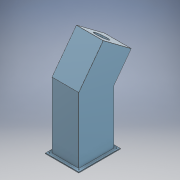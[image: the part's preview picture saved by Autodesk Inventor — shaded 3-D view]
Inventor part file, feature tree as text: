
AUTODESK INVENTOR PART (.ipt)
format: ipt  version: 2022 (Build 260153000, 153)  size: 300,032 bytes
history: native  units: mm
features: sketch x6, extrude x5, fillet x4, chamfer x2, direct_edit x1, plane x1, hole x1, move_body x1
ambient origin geometry x8: Origin, YZ Plane, XZ Plane, XY Plane, X Axis, Y Axis, Z Axis, Center Point
bodies: Solid1 (feature_tree)
feature tree (21):
  extrude  "Extrusion1"  Depth=430.0mm
  direct_edit  "Direct Edit1"
  chamfer  "Chamfer1"  Distance=816.0mm
  chamfer  "Chamfer2"  Distance=400.0mm
  plane  "Work Plane1"
  extrude  "Extrusion2"  Depth=130.0mm
  extrude  "Extrusion3"  Depth=400.0mm TaperAngle=0.0deg
  extrude  "Extrusion4"  Depth=10.0mm TaperAngle=0.0deg
  extrude  "Extrusion5"  Depth=2.0mm
  fillet  "Fillet1"  Radius=2.0mm
  hole  "Hole1"  [1 undecoded]
  fillet  "Fillet2"  [1 undecoded]
  fillet  "Fillet3"  [1 undecoded]
  fillet  "Fillet4"  [1 undecoded]
  sketch  "Sketch1"  dims[d0=330.0mm d1=430.0mm d2=816.0mm d3=0.0mm d6=0.0mm d7=0.0mm d8=400.0mm]
  sketch  "Sketch2"  dims[d9=300.0mm d10=63.5mm d11=9.292133mm d12=130.0mm d13=63.5mm d14=6.41583mm]
  sketch  "Sketch3"  dims[d15=358.4mm d16=0.0mm d17=400.0mm d18=0.0mm]
  sketch  "Sketch4"  dims[d19=10.0mm d20=0.0mm d21=10.0mm d22=0.0mm]
  sketch  "Sketch5"  dims[d23=2.0mm]
  sketch  "Sketch6"  dims[d24=10.106mm d25=24.0mm d26=4.0mm d27=2.0mm d28=90.0deg d29=8.0mm d30=0.0mm d31=2.0mm d32=2.0mm d33=1.0mm d34=0.0mm d35=0.0mm d36=0.0mm]
  move_body  "Move1"
note: 4 required parameter values undecoded (feature->parameter linkage not recoverable at this tier; creation-order binding heuristic only, values carry confidence <= 0.55)
